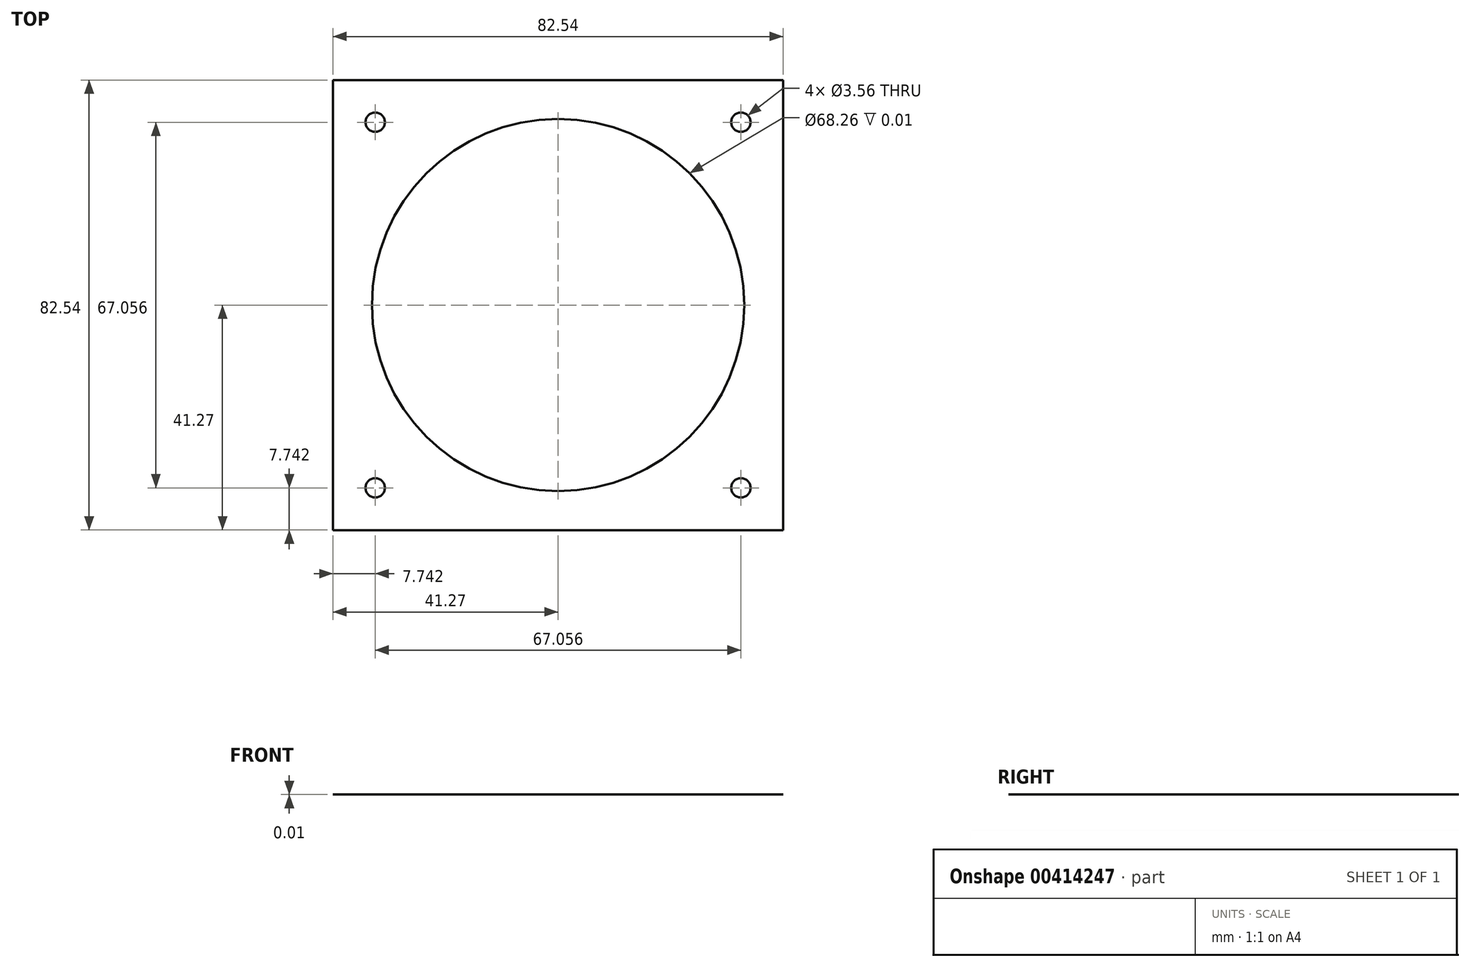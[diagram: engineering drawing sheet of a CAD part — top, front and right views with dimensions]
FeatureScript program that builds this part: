
annotation { "Feature Type Name" : "Feature", "Feature Type Description" : "" }
export const myFeature = defineFeature(function(context is Context, id is Id, definition is map)
    precondition{}
    {
        {
            var Q0;
            Q0=qCreatedBy(makeId("Top.planeOp"),FACE);
            var sketch = newSketch(context, id + "F0", { "sketchPlane" : qUnion([Q0])});
            skLineSegment(sketch, "E0.bottom", {"start": v(41.28, 41.27) * mm, "end": v(-41.28, 41.28) * mm});
            skLineSegment(sketch, "E0.top", {"start": v(41.28, -41.28) * mm, "end": v(-41.28, -41.28) * mm});
            skLineSegment(sketch, "E0.left", {"start": v(41.28, 41.28) * mm, "end": v(41.28, -41.28) * mm});
            skLineSegment(sketch, "E0.right", {"start": v(-41.28, 41.28) * mm, "end": v(-41.28, -41.28) * mm});
            skCircle(sketch, "E1", {"center": v(0, 0) * mm, "radius": 34.13 * mm});
            skLineSegment(sketch, "E2", {"start": v(0, 0) * mm, "end": v(0, 25) * mm, "construction": true});
            skLineSegment(sketch, "E3", {"start": v(0, 25) * mm, "end": v(25, 25) * mm, "construction": true});
            skLineSegment(sketch, "E4", {"start": v(0, 0) * mm, "end": v(41.28, 41.28) * mm, "construction": true});
            skCircle(sketch, "E5", {"center": v(33.53, 33.53) * mm, "radius": 1.78 * mm});
            skCircle(sketch, "E6.1.0", {"center": v(-33.53, 33.53) * mm, "radius": 1.78 * mm});
            skCircle(sketch, "E6.2.0", {"center": v(-33.53, -33.53) * mm, "radius": 1.78 * mm});
            skCircle(sketch, "E6.3.0", {"center": v(33.53, -33.53) * mm, "radius": 1.78 * mm});
            skLineSegment(sketch, "E7", {"start": v(0, 0) * mm, "end": v(41.28, 0) * mm, "construction": true});
            skSolve(sketch);
        }
        {
            var Q0;
            Q0=makeQuery(id+"F0.imprint","IMPRINT",FACE,{"disambiguationData":[TD([[makeQuery(id+"F0.imprint","IMPRINT",EDGE,{"derivedFrom":sQuery(id+"F0.wireOp",EDGE,"E0.bottom")}),1.0]])]});
            extrude(context, id + "F1", {"entities" : qUnion([Q0]), "depth" : 1 / 101.6 * mm});
        }
    });
